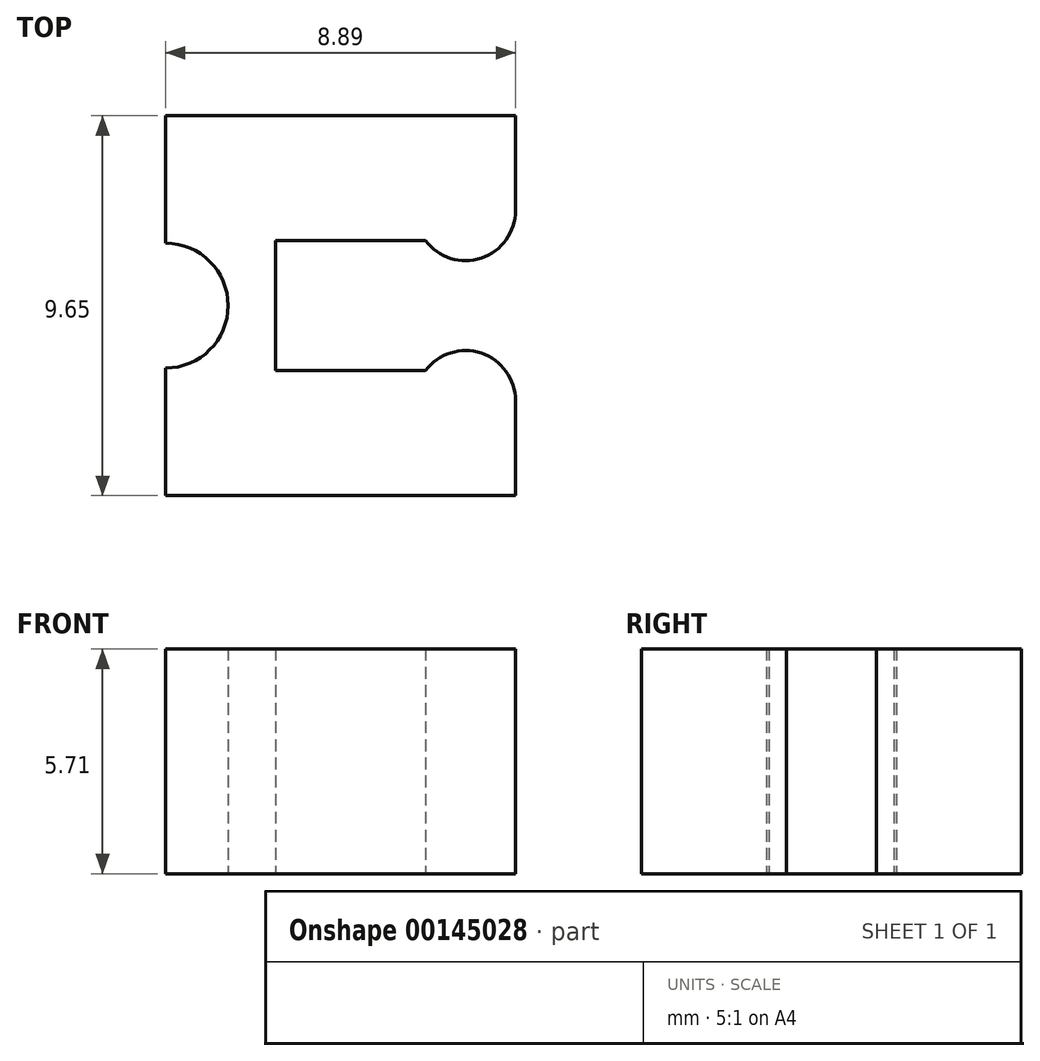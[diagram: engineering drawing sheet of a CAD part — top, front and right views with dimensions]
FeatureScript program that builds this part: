
annotation { "Feature Type Name" : "Feature", "Feature Type Description" : "" }
export const myFeature = defineFeature(function(context is Context, id is Id, definition is map)
    precondition{}
    {
        {
            var Q0;
            Q0=qCreatedBy(makeId("Top.planeOp"),FACE);
            var sketch = newSketch(context, id + "F0", { "sketchPlane" : qUnion([Q0])});
            skLineSegment(sketch, "E0", {"start": v(0, 9.65) * mm, "end": v(0, 6.41) * mm});
            skLineSegment(sketch, "E1", {"start": v(0, 0) * mm, "end": v(8.89, 0) * mm});
            skLineSegment(sketch, "E2", {"start": v(8.89, 0) * mm, "end": v(8.9, 2.41) * mm});
            skLineSegment(sketch, "E3", {"start": v(0, 9.65) * mm, "end": v(8.89, 9.65) * mm});
            skLineSegment(sketch, "E4", {"start": v(8.89, 9.65) * mm, "end": v(8.89, 7.24) * mm});
            skArc(sketch, "E5", {"start": v(8.9, 2.41) * mm, "mid": v(8.02, 3.62) * mm, "end": v(6.6, 3.17) * mm});
            skArc(sketch, "E6", {"start": v(6.6, 6.48) * mm, "mid": v(8.02, 6.03) * mm, "end": v(8.9, 7.24) * mm});
            skLineSegment(sketch, "E7", {"start": v(6.6, 6.48) * mm, "end": v(2.8, 6.48) * mm});
            skLineSegment(sketch, "E8", {"start": v(2.8, 6.48) * mm, "end": v(2.8, 3.18) * mm});
            skLineSegment(sketch, "E9", {"start": v(2.8, 3.18) * mm, "end": v(6.6, 3.17) * mm});
            skArc(sketch, "E10", {"start": v(0, 3.24) * mm, "mid": v(1.59, 4.83) * mm, "end": v(0, 6.41) * mm});
            skLineSegment(sketch, "E11.trimOffspring", {"start": v(0, 3.24) * mm, "end": v(0, 0) * mm});
            skSolve(sketch);
        }
        {
            var Q0;
            Q0=makeQuery(id+"F0.imprint","IMPRINT",FACE,{"disambiguationData":[TD([[makeQuery(id+"F0.imprint","IMPRINT",EDGE,{"derivedFrom":sQuery(id+"F0.wireOp",EDGE,"E0")}),1.0]])]});
            extrude(context, id + "F1", {"entities" : qUnion([Q0]), "depth" : 5.7 * mm});
        }
    });
